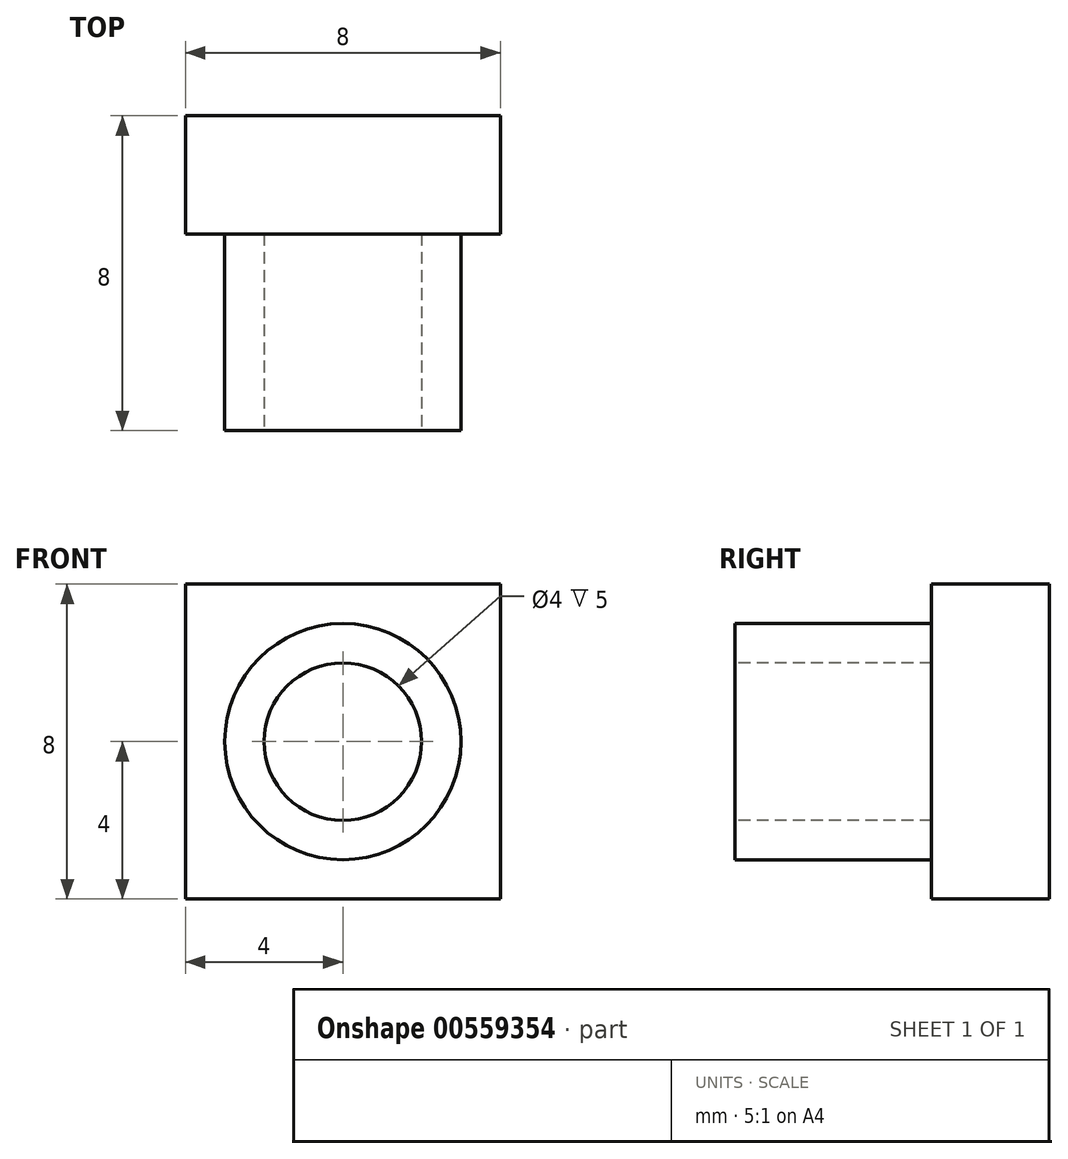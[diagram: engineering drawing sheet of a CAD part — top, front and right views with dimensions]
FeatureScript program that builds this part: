
annotation { "Feature Type Name" : "Feature", "Feature Type Description" : "" }
export const myFeature = defineFeature(function(context is Context, id is Id, definition is map)
    precondition{}
    {
        {
            var Q0;
            Q0=qCreatedBy(makeId("Front.planeOp"),FACE);
            var sketch = newSketch(context, id + "F0", { "sketchPlane" : qUnion([Q0])});
            skLineSegment(sketch, "E0.bottom", {"start": v(-4, 4) * mm, "end": v(4, 4) * mm});
            skLineSegment(sketch, "E0.top", {"start": v(-4, -4) * mm, "end": v(4, -4) * mm});
            skLineSegment(sketch, "E0.left", {"start": v(-4, 4) * mm, "end": v(-4, -4) * mm});
            skLineSegment(sketch, "E0.right", {"start": v(4, 4) * mm, "end": v(4, -4) * mm});
            skPoint(sketch, "E0.middle", {"position": v(0, 0) * mm});
            skSolve(sketch);
        }
        {
            var Q0;
            Q0 = qSketchRegion(id + "F0", true);
            extrude(context, id + "F1", {"entities" : qUnion([Q0]), "depth" : 3 * mm, "offsetDistance" : 25 * mm});
        }
        {
            var Q0;
            Q0=makeQuery(id+"F1.opExtrude","CAP_FACE",FACE,{"disambiguationData":[OSD([sQuery(id+"F0.wireOp",EDGE,"E0.bottom"),sQuery(id+"F0.wireOp",EDGE,"E0.top"),sQuery(id+"F0.wireOp",EDGE,"E0.left"),sQuery(id+"F0.wireOp",EDGE,"E0.right")])],"isStart":false});
            var sketch = newSketch(context, id + "F2", { "sketchPlane" : qUnion([Q0])});
            skCircle(sketch, "E1", {"center": v(0, 0) * mm, "radius": 3 * mm});
            skSolve(sketch);
        }
        {
            var Q0;
            Q0=makeQuery(id+"F2.imprint","IMPRINT",FACE,{"disambiguationData":[TD([[makeQuery(id+"F2.imprint","IMPRINT",EDGE,{"derivedFrom":sQuery(id+"F2.wireOp",EDGE,"E1")}),1.0]])]});
            var Q1;
            Q1=sQuery(id+"F2.wireOp",EDGE,"E1");
            extrude(context, id + "F3", {"entities" : qUnion([Q0]), "surfaceEntities" : qUnion([Q1]), "depth" : 5 * mm, "offsetDistance" : 25 * mm});
        }
        {
            var Q0;
            Q0=makeQuery(id+"F3.opExtrude","CAP_FACE",FACE,{"disambiguationData":[OSD([sQuery(id+"F2.wireOp",EDGE,"E1")])],"isStart":false});
            var sketch = newSketch(context, id + "F4", { "sketchPlane" : qUnion([Q0])});
            skCircle(sketch, "E2", {"center": v(0, 0) * mm, "radius": 2 * mm});
            skSolve(sketch);
        }
        {
            var Q0;
            Q0 = qSketchRegion(id + "F4", true);
            extrude(context, id + "F5", {"entities" : qUnion([Q0]), "operationType" : NewBodyOperationType.REMOVE, "oppositeDirection" : true, "depth" : 5 * mm, "offsetDistance" : 25 * mm});
        }
    });
